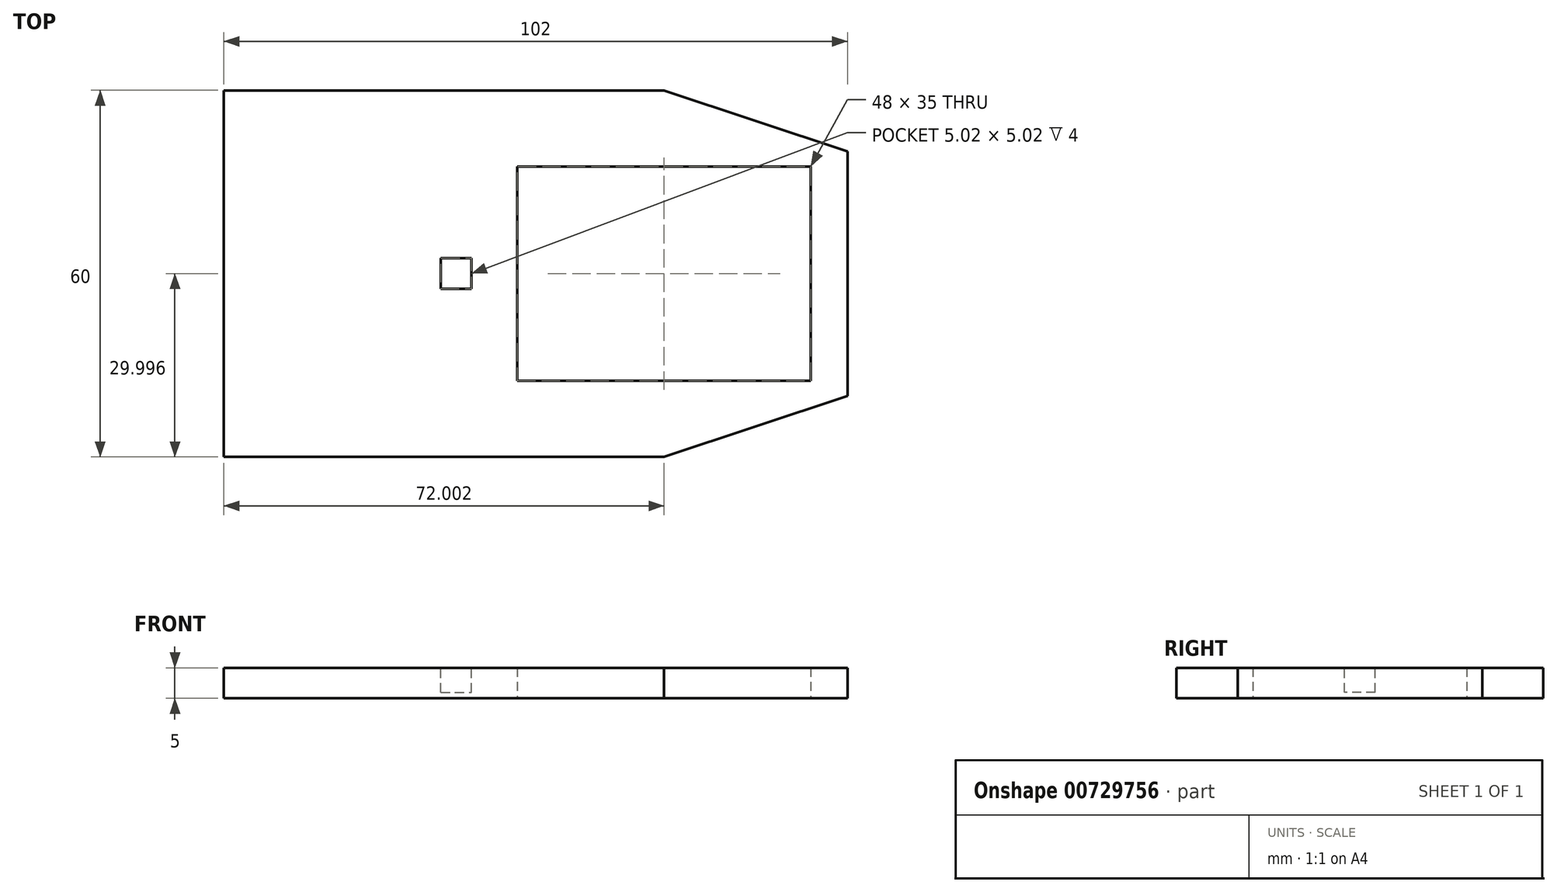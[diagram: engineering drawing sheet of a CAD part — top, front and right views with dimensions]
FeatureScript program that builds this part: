
annotation { "Feature Type Name" : "Feature", "Feature Type Description" : "" }
export const myFeature = defineFeature(function(context is Context, id is Id, definition is map)
    precondition{}
    {
        {
            var Q0;
            Q0=qCreatedBy(makeId("Top.planeOp"),FACE);
            var sketch = newSketch(context, id + "F0", { "sketchPlane" : qUnion([Q0])});
            skLineSegment(sketch, "E0.bottom", {"start": v(-114.9, 61.2) * mm, "end": v(-12.9, 61.2) * mm});
            skLineSegment(sketch, "E0.top", {"start": v(-114.9, 1.2) * mm, "end": v(-12.9, 1.2) * mm});
            skLineSegment(sketch, "E0.left", {"start": v(-114.9, 61.2) * mm, "end": v(-114.9, 1.2) * mm});
            skLineSegment(sketch, "E0.right", {"start": v(-12.9, 61.2) * mm, "end": v(-12.9, 1.2) * mm});
            skLineSegment(sketch, "E1.bottom", {"start": v(-66.9, 48.7) * mm, "end": v(-18.9, 48.7) * mm});
            skLineSegment(sketch, "E1.top", {"start": v(-66.9, 13.7) * mm, "end": v(-18.9, 13.7) * mm});
            skLineSegment(sketch, "E1.left", {"start": v(-66.9, 48.7) * mm, "end": v(-66.9, 13.7) * mm});
            skLineSegment(sketch, "E1.right", {"start": v(-18.9, 48.7) * mm, "end": v(-18.9, 13.7) * mm});
            skSolve(sketch);
        }
        {
            var Q0;
            Q0 = qSketchRegion(id + "F0", true);
            extrude(context, id + "F1", {"entities" : qUnion([Q0]), "depth" : 5 * mm, "offsetDistance" : 25 * mm});
        }
        {
            var Q0;
            Q0=makeQuery(id+"F1.opExtrude","CAP_FACE",FACE,{"disambiguationData":[OSD([sQuery(id+"F0.wireOp",EDGE,"E0.bottom"),sQuery(id+"F0.wireOp",EDGE,"E0.top"),sQuery(id+"F0.wireOp",EDGE,"E0.left"),sQuery(id+"F0.wireOp",EDGE,"E0.right"),sQuery(id+"F0.wireOp",EDGE,"E1.bottom"),sQuery(id+"F0.wireOp",EDGE,"E1.top"),sQuery(id+"F0.wireOp",EDGE,"E1.left"),sQuery(id+"F0.wireOp",EDGE,"E1.right")])],"isStart":false});
            var sketch = newSketch(context, id + "F2", { "sketchPlane" : qUnion([Q0])});
            skLineSegment(sketch, "E2", {"start": v(-66.9, 31.2) * mm, "end": v(-76.9, 31.2) * mm});
            skLineSegment(sketch, "E3.bottom", {"start": v(-79.42, 33.7) * mm, "end": v(-74.4, 33.7) * mm});
            skLineSegment(sketch, "E3.top", {"start": v(-79.42, 28.69) * mm, "end": v(-74.4, 28.69) * mm});
            skLineSegment(sketch, "E3.left", {"start": v(-79.42, 33.7) * mm, "end": v(-79.42, 28.69) * mm});
            skLineSegment(sketch, "E3.right", {"start": v(-74.4, 33.7) * mm, "end": v(-74.4, 28.69) * mm});
            skPoint(sketch, "E3.middle", {"position": v(-76.9, 31.2) * mm});
            skSolve(sketch);
        }
        {
            var Q0;
            Q0 = qSketchRegion(id + "F2", true);
            extrude(context, id + "F3", {"entities" : qUnion([Q0]), "operationType" : NewBodyOperationType.REMOVE, "oppositeDirection" : true, "depth" : 4 * mm, "offsetDistance" : 25 * mm});
        }
        {
            var Q0;
            Q0=makeQuery(id+"F1.opExtrude","SWEPT_EDGE",EDGE,{"disambiguationData":[OSD([sQuery(id+"F0.wireOp",EDGE,"E0.top"),sQuery(id+"F0.wireOp",EDGE,"E0.right")])]});
            var Q1;
            Q1=makeQuery(id+"F1.opExtrude","SWEPT_EDGE",EDGE,{"disambiguationData":[OSD([sQuery(id+"F0.wireOp",EDGE,"E0.bottom"),sQuery(id+"F0.wireOp",EDGE,"E0.right")])]});
            chamfer(context, id + "F4", {"entities" : qUnion([Q0, Q1]), "chamferType" : ChamferType.TWO_OFFSETS, "width1" : 10 * mm, "oppositeDirection" : false, "width2" : 30 * mm, "tangentPropagation" : true});
        }
    });
